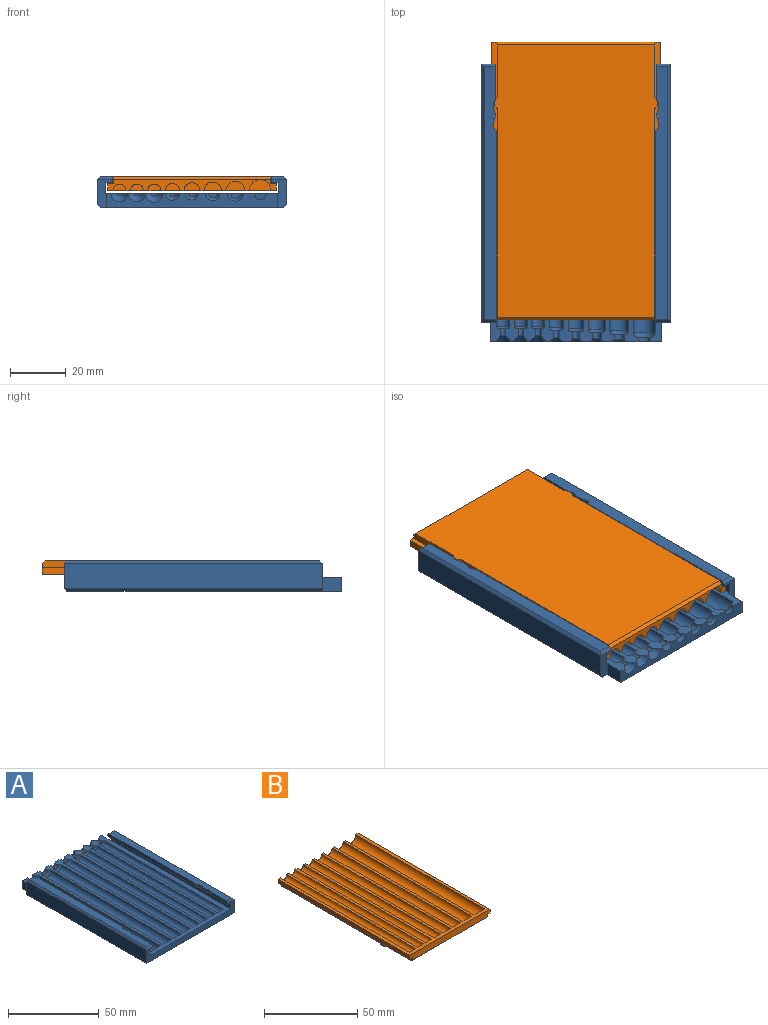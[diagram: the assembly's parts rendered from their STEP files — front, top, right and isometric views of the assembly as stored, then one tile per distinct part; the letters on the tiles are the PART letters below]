
ASSEMBLY  parts=2 mates=1
PART A: 88 faces, bbox 68.1x100x11 mm
  f0: plane 61.74x5mm, normal (0,1,0), area 213.4mm2, adj f1,f10,f11,f12,f37,f46,f47,f48
  f1: plane 100x62.54mm, normal (0,0,1), area 1856mm2, adj f0,f2,f3,f4,f5,f6,f7,f8
  f2: cylinder r=2.34mm len=92mm, axis (0,1,0), area 675.2mm2, adj f1,f21,f43
  f3: cylinder r=2.34mm len=92mm, axis (0,1,0), area 675.2mm2, adj f1,f20,f44
  f4: cylinder r=2.34mm len=92mm, axis (0,1,0), area 675.2mm2, adj f1,f19,f45
  f5: cylinder r=2.59mm len=92.38mm, axis (0,1,0), area 751.9mm2, adj f1,f18,f42
  f6: cylinder r=2.85mm len=92.75mm, axis (0,1,0), area 829.3mm2, adj f1,f17,f41
  f7: cylinder r=3.1mm len=93.13mm, axis (0,1,0), area 907.2mm2, adj f1,f16,f40
  f8: cylinder r=3.41mm len=93.58mm, axis (0,1,0), area 1001.6mm2, adj f1,f15,f39
  f9: cylinder r=3.92mm len=94.33mm, axis (0,1,0), area 1160.7mm2, adj f1,f14,f38
  f10: plane 7x5mm, normal (-1,0,0), area 35mm2, adj f0,f1,f11,f53
  f11: plane 99x66.14mm, normal (0,0,-1), area 6517.1mm2, adj f0,f10,f12,f53,f63,f79,f80,f81
  f12: plane 7x5mm, normal (1,0,0), area 35mm2, adj f0,f1,f11,f63
  f13: plane 68.14x9mm, normal (0,-1,0), area 304.8mm2, adj f1,f54,f55,f58,f59,f64,f65,f68
  f14: plane 7.83x3.92mm, normal (0,1,0), area 24.1mm2, adj f1,f9
  f15: plane 6.81x3.41mm, normal (0,1,0), area 18.2mm2, adj f1,f8
  f16: plane 6.2x3.1mm, normal (0,1,0), area 15.1mm2, adj f1,f7
  f17: plane 5.69x2.85mm, normal (0,1,0), area 12.7mm2, adj f1,f6
  f18: plane 5.18x2.59mm, normal (0,1,0), area 10.5mm2, adj f1,f5
  f19: plane 4.67x2.34mm, normal (0,1,0), area 8.6mm2, adj f1,f4
  f20: plane 4.67x2.34mm, normal (0,1,0), area 8.6mm2, adj f1,f3
  f21: plane 4.67x2.34mm, normal (0,1,0), area 8.6mm2, adj f1,f2
  f22: plane 4.48x2.24mm, normal (0,-1,0), area 0.2mm2, adj f1,f37,f38
  f23: plane 3.96x1.98mm, normal (0,-1,0), area 0.7mm2, adj f1,f36,f39
  f24: plane 3.65x1.83mm, normal (0,-1,0), area 1.4mm2, adj f1,f35,f40
  f25: plane 3.39x1.7mm, normal (0,-1,0), area 2mm2, adj f1,f34,f41
  f26: plane 3.13x1.57mm, normal (0,-1,0), area 1.7mm2, adj f1,f33,f42
  f27: plane 2.87x1.44mm, normal (0,-1,0), area 1.9mm2, adj f1,f32,f43
  f28: plane 2.87x1.44mm, normal (0,-1,0), area 1.9mm2, adj f1,f31,f44
  f29: plane 2.87x1.44mm, normal (0,-1,0), area 1.5mm2, adj f1,f30,f45
  f30: cylinder r=1.06mm len=2.55mm, axis (0,-1,0), area 8.5mm2, adj f1,f29,f46
  f31: cylinder r=0.91mm len=2.55mm, axis (0,-1,0), area 7.3mm2, adj f1,f28,f47
  f32: cylinder r=0.91mm len=2.55mm, axis (0,-1,0), area 7.3mm2, adj f1,f27,f48
  f33: cylinder r=1.16mm len=2.83mm, axis (0,-1,0), area 10.3mm2, adj f1,f26,f49
  f34: cylinder r=1.26mm len=2.55mm, axis (0,-1,0), area 10.1mm2, adj f1,f25,f50
  f35: cylinder r=1.56mm len=3.13mm, axis (0,-1,0), area 10.7mm2, adj f1,f24,f51
  f36: cylinder r=1.87mm len=3.73mm, axis (0,-1,0), area 9.7mm2, adj f1,f23,f52
  f37: cylinder r=2.22mm len=4.44mm, axis (0,-1,0), area 11.2mm2, adj f0,f1,f22
  f38: torus R=2.24mm, axis (0,1,0), area 27.3mm2, adj f1,f9,f22
  f39: torus R=1.98mm, axis (0,1,0), area 20.3mm2, adj f1,f8,f23
  f40: torus R=1.83mm, axis (0,1,0), area 16.6mm2, adj f1,f7,f24
  f41: torus R=1.7mm, axis (0,1,0), area 13.8mm2, adj f1,f6,f25
  f42: torus R=1.57mm, axis (0,1,0), area 11.2mm2, adj f1,f5,f26
  f43: torus R=1.44mm, axis (0,1,0), area 8.9mm2, adj f1,f2,f27
  f44: torus R=1.44mm, axis (0,1,0), area 8.9mm2, adj f1,f3,f28
  f45: torus R=1.44mm, axis (0,1,0), area 8.9mm2, adj f1,f4,f29
  f46: cone r=1.06mm half-angle=45deg, axis (0,1,0), area 20.4mm2, adj f0,f1,f30
  f47: cone r=0.91mm half-angle=45deg, axis (0,1,0), area 18.9mm2, adj f0,f1,f31
  f48: cone r=0.91mm half-angle=45deg, axis (0,1,0), area 18.9mm2, adj f0,f1,f32
  f49: cone r=1.16mm half-angle=45deg, axis (0,1,0), area 11.2mm2, adj f0,f1,f33
  f50: cone r=1.26mm half-angle=45deg, axis (0,1,0), area 9.4mm2, adj f0,f1,f34
  f51: cone r=1.56mm half-angle=45deg, axis (0,1,0), area 9.4mm2, adj f0,f1,f35
  f52: cone r=1.87mm half-angle=45deg, axis (0,1,0), area 9.9mm2, adj f0,f1,f36
  f53: plane 10x5.3mm, normal (0,1,0), area 32mm2, adj f1,f10,f11,f54,f55,f56,f58,f75
  f54: plane 93x4mm, normal (1,0,0), area 372mm2, adj f1,f13,f53,f55
  f55: plane 93x2.5mm, normal (0,0,-1), area 220mm2, adj f13,f53,f54,f56,f59,f60,f61,f62
  f56: plane 69x2mm, normal (1,0,0), area 137.5mm2, adj f53,f55,f57,f61,f75
  f57: plane 91x4.3mm, normal (0,0,1), area 379.3mm2, adj f56,f59,f60,f61,f62,f73,f74,f75
  f58: plane 93x9mm, normal (-1,0,0), area 837mm2, adj f13,f53,f74,f79
  f59: plane 12.76x2mm, normal (1,0,0), area 25mm2, adj f13,f55,f57,f73,f83
  f60: cylinder r=2.5mm len=2.23mm, axis (0,0,1), area 4.6mm2, adj f55,f57,f83,f86
  f61: cylinder r=2.5mm len=2.98mm, axis (0,0,1), area 6.7mm2, adj f55,f56,f57,f87
  f62: plane 2x1.12mm, normal (1,0,0), area 2.2mm2, adj f55,f57,f86,f87
  f63: plane 10x5.3mm, normal (0,1,0), area 32mm2, adj f1,f11,f12,f64,f65,f66,f68,f78
  f64: plane 93x4mm, normal (-1,0,0), area 372mm2, adj f1,f13,f63,f65
  f65: plane 93x2.5mm, normal (0,0,-1), area 220mm2, adj f13,f63,f64,f66,f69,f70,f71,f72
  f66: plane 69x2mm, normal (-1,0,0), area 137.5mm2, adj f63,f65,f67,f71,f78
  f67: plane 91x4.3mm, normal (0,0,1), area 379.3mm2, adj f66,f69,f70,f71,f72,f76,f77,f78
  f68: plane 93x9mm, normal (1,0,0), area 837mm2, adj f13,f63,f77,f80
  f69: plane 12.76x2mm, normal (-1,0,0), area 25mm2, adj f13,f65,f67,f76,f82
  f70: cylinder r=2.5mm len=2.23mm, axis (0,0,1), area 4.6mm2, adj f65,f67,f82,f84
  f71: cylinder r=2.5mm len=2.98mm, axis (0,0,1), area 6.7mm2, adj f65,f66,f67,f85
  f72: plane 2x1.12mm, normal (-1,0,0), area 2.2mm2, adj f65,f67,f84,f85
  f73: plane 4.9x1mm, normal (0,-0.71,0.71), area 6.2mm2, adj f13,f57,f59,f74
  f74: plane 93x1mm, normal (-0.71,0,0.71), area 130.1mm2, adj f57,f58,f73,f75
  f75: plane 5.3x1mm, normal (0,0.71,0.71), area 6.8mm2, adj f53,f56,f57,f74
  f76: plane 4.9x1mm, normal (0,-0.71,0.71), area 6.2mm2, adj f13,f67,f69,f77
  f77: plane 93x1mm, normal (0.71,0,0.71), area 130.1mm2, adj f67,f68,f76,f78
  f78: plane 5.3x1mm, normal (0,0.71,0.71), area 6.8mm2, adj f63,f66,f67,f77
  f79: plane 93x1mm, normal (-0.71,0,-0.71), area 130.8mm2, adj f11,f53,f58,f81
  f80: plane 93x1mm, normal (0.71,0,-0.71), area 130.8mm2, adj f11,f63,f68,f81
  f81: plane 68.14x1mm, normal (0,-0.71,-0.71), area 95mm2, adj f11,f13,f79,f80
  f82: cylinder r=2mm len=2mm, axis (0,0,1), area 2.1mm2, adj f65,f67,f69,f70
  f83: cylinder r=2mm len=2mm, axis (0,0,1), area 2.1mm2, adj f55,f57,f59,f60
  f84: cylinder r=5mm len=2mm, axis (0,0,1), area 4mm2, adj f65,f67,f70,f72
  f85: cylinder r=5mm len=2mm, axis (0,0,1), area 4mm2, adj f65,f67,f71,f72
  f86: cylinder r=5mm len=2mm, axis (0,0,1), area 4mm2, adj f55,f57,f60,f62
  f87: cylinder r=5mm len=2mm, axis (0,0,1), area 4mm2, adj f55,f57,f61,f62
PART B: 32 faces, bbox 60.7x100x5 mm
  f0: plane 100x60.74mm, normal (0,0,1), area 1609.8mm2, adj f1,f2,f6,f7,f8,f9,f10,f11
  f1: plane 60.74x4mm, normal (0,-1,0), area 237mm2, adj f0,f3,f4,f22,f24,f26,f30,f31
  f2: plane 60.74x4mm, normal (0,1,0), area 130.5mm2, adj f0,f6,f7,f8,f9,f10,f11,f12
  f3: plane 20x2.5mm, normal (-1,0,0), area 49.5mm2, adj f1,f5,f24,f26,f29
  f4: plane 20x2.5mm, normal (1,0,0), area 49.5mm2, adj f1,f5,f22,f26,f28
  f5: plane 98x58.74mm, normal (0,0,-1), area 5566.1mm2, adj f3,f4,f23,f25,f26,f27,f28,f29
  f6: cylinder r=2.34mm len=97.6mm, axis (0,1,0), area 716.3mm2, adj f0,f2,f21
  f7: cylinder r=2.34mm len=97.6mm, axis (0,1,0), area 716.3mm2, adj f0,f2,f20
  f8: cylinder r=2.34mm len=97.6mm, axis (0,1,0), area 716.3mm2, adj f0,f2,f19
  f9: cylinder r=2.59mm len=97.6mm, axis (0,1,0), area 794.5mm2, adj f0,f2,f18
  f10: cylinder r=2.85mm len=97.6mm, axis (0,1,0), area 872.6mm2, adj f0,f2,f17
  f11: cylinder r=3.1mm len=97.6mm, axis (0,1,0), area 950.8mm2, adj f0,f2,f16
  f12: cylinder r=3.41mm len=97.6mm, axis (0,1,0), area 1044.7mm2, adj f0,f2,f15
  f13: cylinder r=3.92mm len=97.6mm, axis (0,1,0), area 1201mm2, adj f0,f2,f14
  f14: plane 7.83x3.92mm, normal (0,1,0), area 24.1mm2, adj f0,f13
  f15: plane 6.81x3.41mm, normal (0,1,0), area 18.2mm2, adj f0,f12
  f16: plane 6.2x3.1mm, normal (0,1,0), area 15.1mm2, adj f0,f11
  f17: plane 5.69x2.85mm, normal (0,1,0), area 12.7mm2, adj f0,f10
  f18: plane 5.18x2.59mm, normal (0,1,0), area 10.5mm2, adj f0,f9
  f19: plane 4.67x2.34mm, normal (0,1,0), area 8.6mm2, adj f0,f8
  f20: plane 4.67x2.34mm, normal (0,1,0), area 8.6mm2, adj f0,f7
  f21: plane 4.67x2.34mm, normal (0,1,0), area 8.6mm2, adj f0,f6
  f22: plane 100x2mm, normal (0,0,-1), area 197.2mm2, adj f1,f2,f4,f23,f28,f31
  f23: plane 76x2.5mm, normal (1,0,0), area 189.5mm2, adj f2,f5,f22,f27,f28
  f24: plane 100x2mm, normal (0,0,-1), area 197.2mm2, adj f1,f2,f3,f25,f29,f30
  f25: plane 76x2.5mm, normal (-1,0,0), area 189.5mm2, adj f2,f5,f24,f27,f29
  f26: plane 56.74x1mm, normal (0,-0.71,-0.71), area 80.2mm2, adj f1,f3,f4,f5
  f27: plane 56.74x1mm, normal (0,0.71,-0.71), area 80.2mm2, adj f2,f5,f23,f25
  f28: cylinder r=2.5mm len=4mm, axis (0,0,-1), area 11.6mm2, adj f4,f5,f22,f23
  f29: cylinder r=2.5mm len=4mm, axis (0,0,-1), area 11.6mm2, adj f3,f5,f24,f25
  f30: plane 100x2.5mm, normal (-1,0,0), area 250mm2, adj f0,f1,f2,f24
  f31: plane 100x2.5mm, normal (1,0,0), area 250mm2, adj f0,f1,f2,f22
PLACE A rot(axis=(0,0,1),180deg) t=(0,0.28,2.5)mm
PLACE B rot(axis=(1,0,0),180deg) t=(-69.74,8.16,8.5)mm
MATE slider B.f2 <-> A.f0  axis (0,-1,0) through (0,-41.84,10)mm
